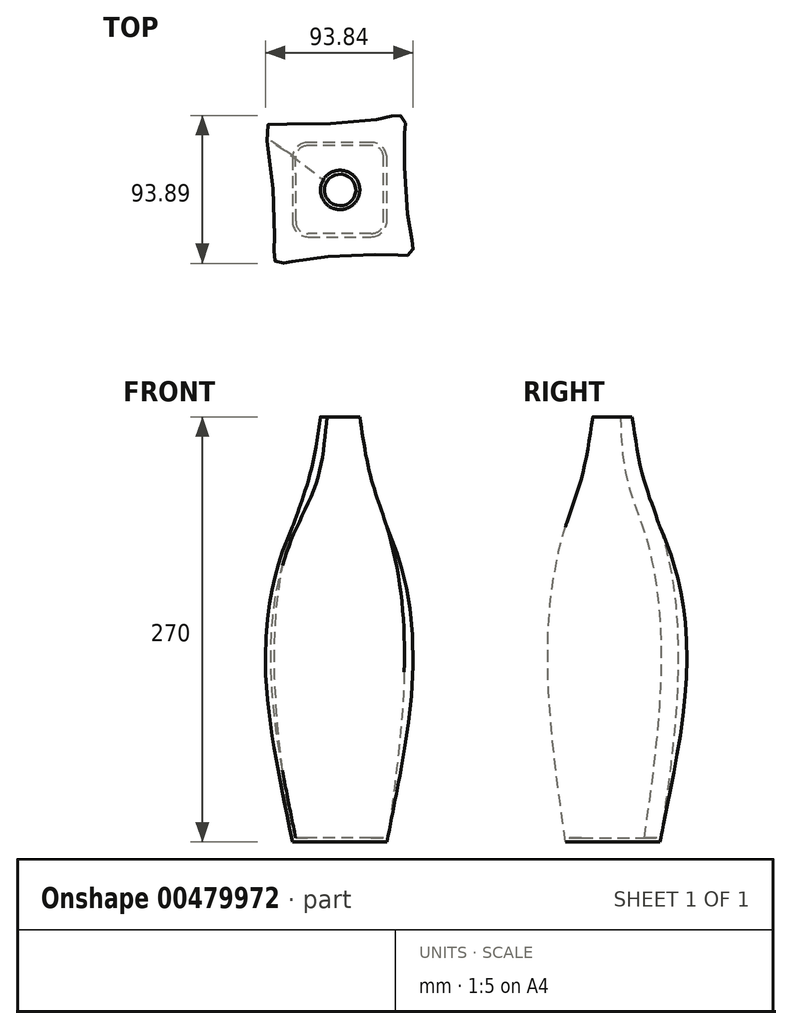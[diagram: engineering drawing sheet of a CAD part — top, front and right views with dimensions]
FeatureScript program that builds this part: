
annotation { "Feature Type Name" : "Feature", "Feature Type Description" : "" }
export const myFeature = defineFeature(function(context is Context, id is Id, definition is map)
    precondition{}
    {
        {
            var Q0;
            Q0=qCreatedBy(makeId("Top.planeOp"),FACE);
            var sketch = newSketch(context, id + "F0", { "sketchPlane" : qUnion([Q0])});
            skLineSegment(sketch, "E0", {"start": v(-25.58, 28.04) * mm, "end": v(-25.58, -11.96) * mm});
            skLineSegment(sketch, "E1", {"start": v(-15.58, -21.96) * mm, "end": v(24.42, -21.96) * mm});
            skLineSegment(sketch, "E2", {"start": v(34.42, -11.96) * mm, "end": v(34.42, 28.04) * mm});
            skLineSegment(sketch, "E3", {"start": v(24.42, 38.04) * mm, "end": v(-15.58, 38.04) * mm});
            skPoint(sketch, "E4.visualSharp", {"position": v(-25.58, 38.04) * mm});
            skArc(sketch, "E4.filletArc", {"start": v(-15.58, 38.04) * mm, "mid": v(-22.65, 35.1) * mm, "end": v(-25.58, 28.04) * mm});
            skPoint(sketch, "E5.visualSharp", {"position": v(34.42, 38.04) * mm});
            skArc(sketch, "E5.filletArc", {"start": v(34.42, 28.04) * mm, "mid": v(31.5, 35.1) * mm, "end": v(24.42, 38.04) * mm});
            skPoint(sketch, "E6.visualSharp", {"position": v(34.42, -21.96) * mm});
            skArc(sketch, "E6.filletArc", {"start": v(24.42, -21.96) * mm, "mid": v(31.5, -19.04) * mm, "end": v(34.42, -11.96) * mm});
            skPoint(sketch, "E7.visualSharp", {"position": v(-25.58, -21.96) * mm});
            skArc(sketch, "E7.filletArc", {"start": v(-25.58, -11.96) * mm, "mid": v(-22.65, -19.04) * mm, "end": v(-15.58, -21.96) * mm});
            skSolve(sketch);
        }
        {
            var Q0;
            Q0=makeQuery(id+"F0.imprint","IMPRINT",FACE,{"disambiguationData":[TD([[makeQuery(id+"F0.imprint","IMPRINT",EDGE,{"derivedFrom":sQuery(id+"F0.wireOp",EDGE,"E0")}),1.0]])]});
            cPlane(context, id + "F1", {"entities" : qUnion([Q0]), "cplaneType" : CPlaneType.OFFSET, "offset" : 200 * mm, "width" : 150 * mm, "height" : 150 * mm});
        }
        {
            var Q0;
            Q0=qCreatedBy(id+"F1.planeOp",FACE);
            var sketch = newSketch(context, id + "F2", { "sketchPlane" : qUnion([Q0])});
            skLineSegment(sketch, "E8", {"start": v(-15.55, 37.9) * mm, "end": v(24.42, 37.9) * mm});
            skLineSegment(sketch, "E9", {"start": v(34.42, 27.9) * mm, "end": v(34.42, -12.1) * mm});
            skLineSegment(sketch, "E10", {"start": v(24.42, -22.1) * mm, "end": v(-15.42, -22.1) * mm});
            skLineSegment(sketch, "E11", {"start": v(-25.42, -12.13) * mm, "end": v(-25.55, 27.87) * mm});
            skPoint(sketch, "E12.visualSharp", {"position": v(-25.58, 37.9) * mm});
            skArc(sketch, "E12.filletArc", {"start": v(-15.55, 37.9) * mm, "mid": v(-22.63, 34.96) * mm, "end": v(-25.55, 27.87) * mm});
            skPoint(sketch, "E13.visualSharp", {"position": v(34.42, 37.9) * mm});
            skArc(sketch, "E13.filletArc", {"start": v(34.42, 27.9) * mm, "mid": v(31.5, 34.97) * mm, "end": v(24.42, 37.9) * mm});
            skPoint(sketch, "E14.visualSharp", {"position": v(34.42, -22.1) * mm});
            skArc(sketch, "E14.filletArc", {"start": v(24.42, -22.1) * mm, "mid": v(31.5, -19.17) * mm, "end": v(34.42, -12.1) * mm});
            skPoint(sketch, "E15.visualSharp", {"position": v(-25.4, -22.1) * mm});
            skArc(sketch, "E15.filletArc", {"start": v(-25.42, -12.13) * mm, "mid": v(-22.48, -19.18) * mm, "end": v(-15.42, -22.1) * mm});
            skSolve(sketch);
        }
        {
            var Q0;
            Q0=makeQuery(id+"F2.imprint","IMPRINT",FACE,{"disambiguationData":[TD([[makeQuery(id+"F2.imprint","IMPRINT",EDGE,{"derivedFrom":sQuery(id+"F2.wireOp",EDGE,"E8")}),-1.0]])]});
            cPlane(context, id + "F3", {"entities" : qUnion([Q0]), "cplaneType" : CPlaneType.OFFSET, "offset" : 30 * mm, "width" : 150 * mm, "height" : 150 * mm});
        }
        {
            var Q0;
            Q0=qCreatedBy(id+"F3.planeOp",FACE);
            var sketch = newSketch(context, id + "F4", { "sketchPlane" : qUnion([Q0])});
            skCircle(sketch, "E16", {"center": v(4.67, 7.77) * mm, "radius": 20 * mm});
            skPoint(sketch, "E17.orphan", {"position": v(40.67, 44) * mm});
            skPoint(sketch, "E18.end.orphan", {"position": v(-30.88, -28) * mm});
            skPoint(sketch, "E19.trimOffspring.end.orphan", {"position": v(40.67, -28) * mm});
            skSolve(sketch);
        }
        {
            var Q0;
            Q0=makeQuery(id+"F4.imprint","IMPRINT",FACE,{"disambiguationData":[TD([[makeQuery(id+"F4.imprint","IMPRINT",EDGE,{"derivedFrom":sQuery(id+"F4.wireOp",EDGE,"E16")}),1.0]])]});
            cPlane(context, id + "F5", {"entities" : qUnion([Q0]), "cplaneType" : CPlaneType.OFFSET, "offset" : 40 * mm, "width" : 150 * mm, "height" : 150 * mm});
        }
        {
            var Q0;
            Q0=qCreatedBy(id+"F5.planeOp",FACE);
            var sketch = newSketch(context, id + "F6", { "sketchPlane" : qUnion([Q0])});
            skCircle(sketch, "E20", {"center": v(4.7, 7.8) * mm, "radius": 12.5 * mm});
            skSolve(sketch);
        }
        {
            var Q0;
            Q0=makeQuery(id+"F0.imprint","IMPRINT",FACE,{"disambiguationData":[TD([[makeQuery(id+"F0.imprint","IMPRINT",EDGE,{"derivedFrom":sQuery(id+"F0.wireOp",EDGE,"E0")}),1.0]])]});
            var Q1;
            Q1=makeQuery(id+"F2.imprint","IMPRINT",FACE,{"disambiguationData":[TD([[makeQuery(id+"F2.imprint","IMPRINT",EDGE,{"derivedFrom":sQuery(id+"F2.wireOp",EDGE,"E8")}),-1.0]])]});
            var Q2;
            Q2=makeQuery(id+"F4.imprint","IMPRINT",FACE,{"disambiguationData":[TD([[makeQuery(id+"F4.imprint","IMPRINT",EDGE,{"derivedFrom":sQuery(id+"F4.wireOp",EDGE,"E16")}),1.0]])]});
            var Q3;
            Q3=makeQuery(id+"F6.imprint","IMPRINT",FACE,{"disambiguationData":[TD([[makeQuery(id+"F6.imprint","IMPRINT",EDGE,{"derivedFrom":sQuery(id+"F6.wireOp",EDGE,"E20")}),1.0]])]});
            loft(context, id + "F7", {"sheetProfilesArray" : [{ "sheetProfileEntities" : qUnion([Q0]) }, { "sheetProfileEntities" : qUnion([Q1]) }, { "sheetProfileEntities" : qUnion([Q2]) }, { "sheetProfileEntities" : qUnion([Q3]) }]});
        }
        {
            var Q0;
            Q0=makeQuery(id+"F7.opLoft","CAP_FACE",FACE,{"disambiguationData":[OSD([makeQuery(id+"F6.imprint","IMPRINT",FACE,{"disambiguationData":[TD([[makeQuery(id+"F6.imprint","IMPRINT",EDGE,{"derivedFrom":sQuery(id+"F6.wireOp",EDGE,"E20")}),1.0]])]})])],"isStart":true});
            shell(context, id + "F8", {"entities" : qUnion([Q0]), "thickness" : 2.5 * mm});
        }
    });
